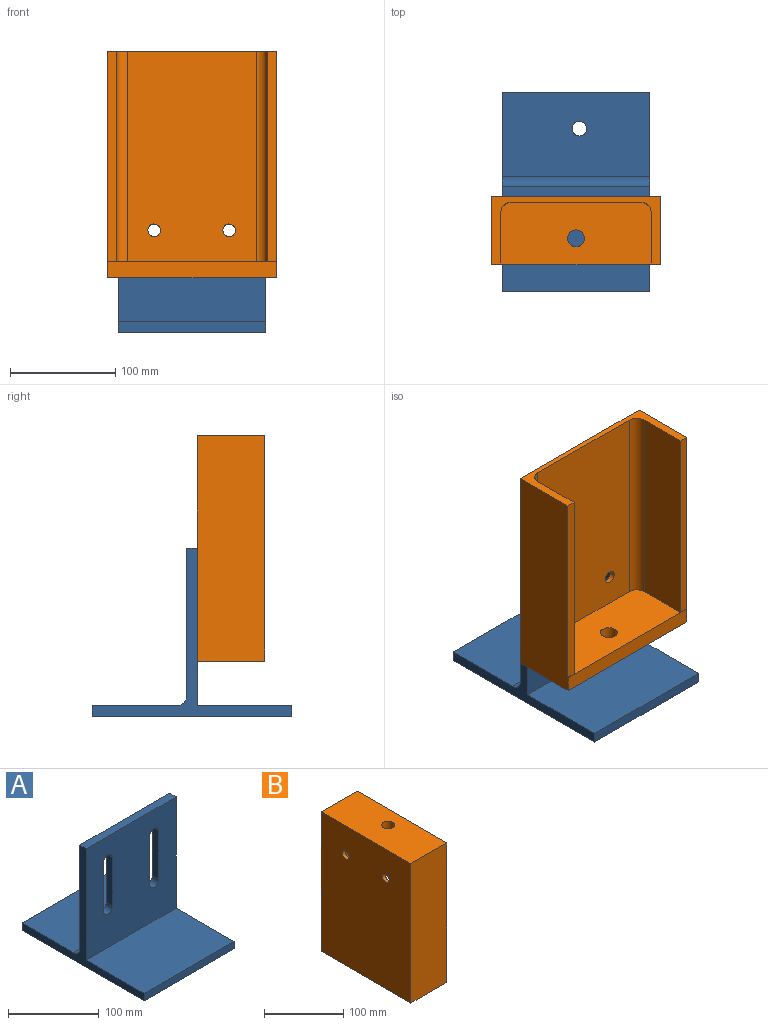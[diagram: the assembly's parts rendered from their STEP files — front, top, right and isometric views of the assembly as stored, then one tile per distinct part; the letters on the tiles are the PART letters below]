
ASSEMBLY  parts=2 mates=1
PART A: 20 faces, bbox 140x190x160 mm
  f0: plane 190x140mm, normal (0,0,-1), area 26446.1mm2, adj f1,f7,f8,f9,f19
  f1: plane 140x10mm, normal (0,1,0), area 1400mm2, adj f0,f2,f8,f9
  f2: plane 140x80mm, normal (0,0,1), area 11046.1mm2, adj f1,f8,f9,f10,f19
  f3: plane 140x140mm, normal (0,1,0), area 17444.1mm2, adj f4,f8,f9,f10,f11,f12,f13,f14
  f4: plane 140x10mm, normal (0,0,1), area 1400mm2, adj f3,f5,f8,f9
  f5: plane 150x140mm, normal (0,-1,0), area 18844.1mm2, adj f4,f6,f8,f9,f11,f12,f13,f14
  f6: plane 140x90mm, normal (0,0,1), area 12600mm2, adj f5,f7,f8,f9
  f7: plane 140x10mm, normal (0,-1,0), area 1400mm2, adj f0,f6,f8,f9
  f8: plane 190x160mm, normal (1,0,0), area 3421.5mm2, adj f0,f1,f2,f3,f4,f5,f6,f7
  f9: plane 190x160mm, normal (-1,0,0), area 3421.5mm2, adj f0,f1,f2,f3,f4,f5,f6,f7
  f10: cylinder r=10mm len=140mm, axis (1,0,0), area 2199.1mm2, adj f2,f3,f8,f9
  f11: cylinder r=7mm len=14mm, axis (0,1,0), area 219.9mm2, adj f3,f5,f12,f14
  f12: plane 66x10mm, normal (-1,0,0), area 660mm2, adj f3,f5,f11,f13
  f13: cylinder r=7mm len=14mm, axis (0,1,0), area 219.9mm2, adj f3,f5,f12,f14
  f14: plane 66x10mm, normal (1,0,0), area 660mm2, adj f3,f5,f11,f13
  f15: cylinder r=7mm len=14mm, axis (0,1,0), area 219.9mm2, adj f3,f5,f16,f18
  f16: plane 66x10mm, normal (-1,0,0), area 660mm2, adj f3,f5,f15,f17
  f17: cylinder r=7mm len=14mm, axis (0,1,0), area 219.9mm2, adj f3,f5,f16,f18
  f18: plane 66x10mm, normal (1,0,0), area 660mm2, adj f3,f5,f15,f17
  f19: cylinder r=7mm len=14mm, axis (0,0,1), area 439.8mm2, adj f0,f2
PART B: 17 faces, bbox 64.2x160x215 mm
  f0: plane 200x49mm, normal (0,1,0), area 9800mm2, adj f7,f8,f12,f16
  f1: plane 200x123.2mm, normal (1,0,0), area 24413.8mm2, adj f8,f12,f13,f14,f15,f16
  f2: plane 200x49mm, normal (0,-1,0), area 9800mm2, adj f3,f8,f12,f15
  f3: plane 200x8.4mm, normal (1,0,0), area 1680mm2, adj f2,f4,f8,f12
  f4: plane 215x64.23mm, normal (0,1,0), area 13763.5mm2, adj f3,f5,f8,f9,f11,f12
  f5: plane 215x160mm, normal (-1,0,0), area 34173.8mm2, adj f4,f6,f8,f11,f13,f14
  f6: plane 215x64.23mm, normal (0,-1,0), area 13763.5mm2, adj f5,f7,f8,f9,f11,f12
  f7: plane 200x8.4mm, normal (1,0,0), area 1680mm2, adj f0,f6,f8,f12
  f8: plane 160x64mm, normal (0,0,-1), area 1834.1mm2, adj f0,f1,f2,f3,f4,f5,f6,f7
  f9: plane 160x15mm, normal (1,0,0), area 2400mm2, adj f4,f6,f11,f12
  f10: cylinder r=8mm len=16mm, axis (0,0,-1), area 754mm2, adj f11,f12
  f11: plane 160x64.23mm, normal (0,0,1), area 10076.3mm2, adj f4,f5,f6,f9,f10
  f12: plane 160x59.23mm, normal (0,0,-1), area 8242.2mm2, adj f0,f1,f2,f3,f4,f6,f7,f9
  f13: cylinder r=6mm len=12mm, axis (-1,0,0), area 188.5mm2, adj f1,f5
  f14: cylinder r=6mm len=12mm, axis (-1,0,0), area 188.5mm2, adj f1,f5
  f15: cylinder r=10mm len=200mm, axis (0,0,1), area 3141.6mm2, adj f1,f2,f8,f12
  f16: cylinder r=10mm len=200mm, axis (0,0,-1), area 3141.6mm2, adj f0,f1,f8,f12
PLACE A t=(-62.59,-39.64,3.15)mm
PLACE B rot(axis=(0.71,-0.71,0),180deg) t=(-72.59,-39.64,-89.76)mm
MATE parallel B.f5 <-> A.f5  axis (0,1,0) through (7.41,-39.64,3.15)mm
